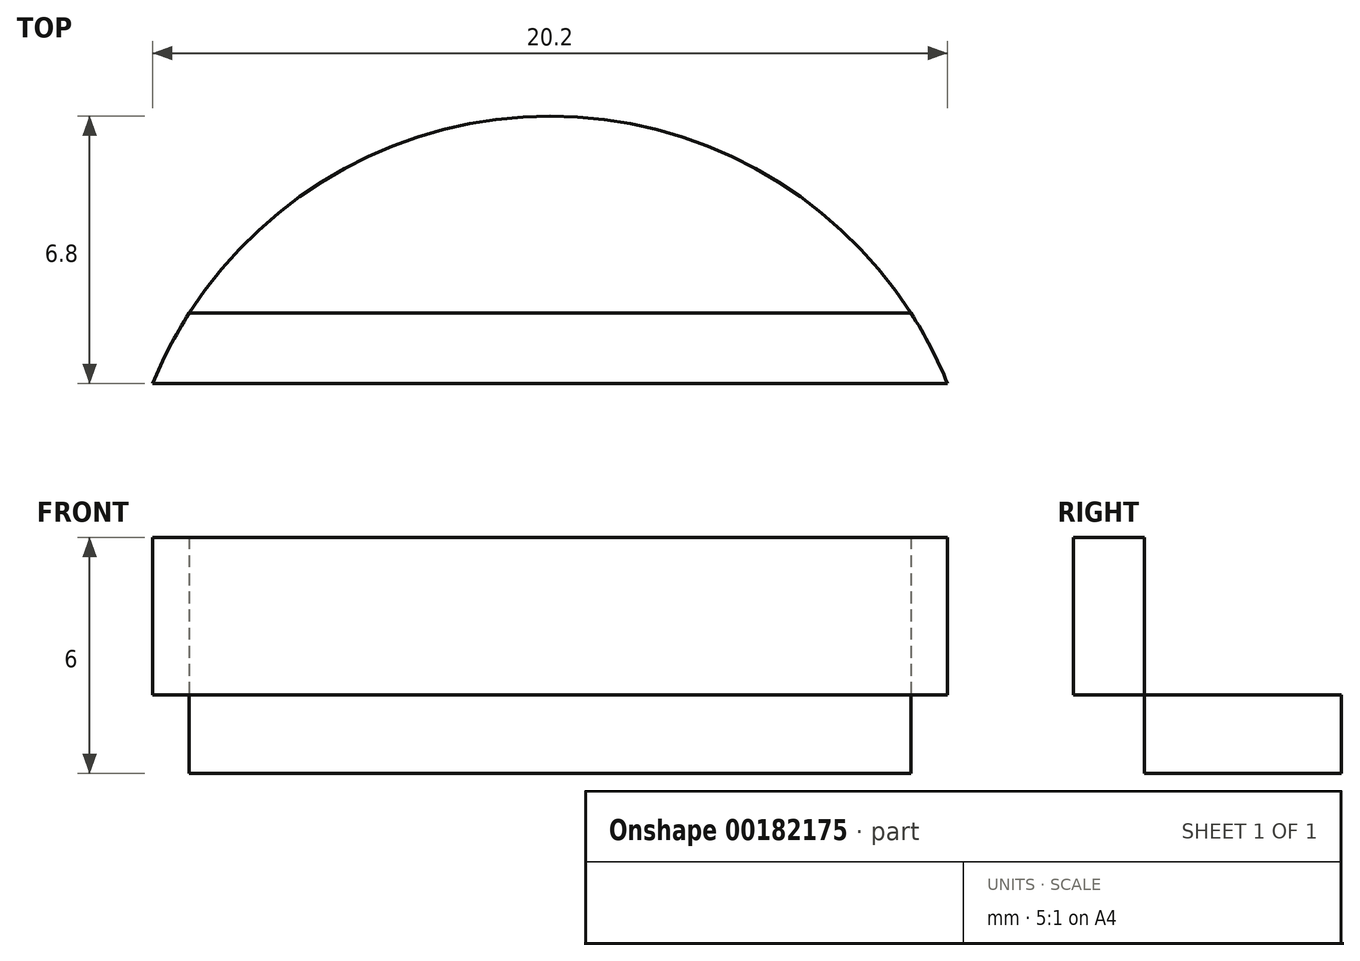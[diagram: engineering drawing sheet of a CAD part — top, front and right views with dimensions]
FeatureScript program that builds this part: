
annotation { "Feature Type Name" : "Feature", "Feature Type Description" : "" }
export const myFeature = defineFeature(function(context is Context, id is Id, definition is map)
    precondition{}
    {
        {
            var Q0;
            Q0=qCreatedBy(makeId("Top.planeOp"),FACE);
            var sketch = newSketch(context, id + "F0", { "sketchPlane" : qUnion([Q0])});
            skCircle(sketch, "E0", {"center": v(0, 0) * mm, "radius": 10.9 * mm});
            skLineSegment(sketch, "E1.bottom", {"start": v(17.66, -5.9) * mm, "end": v(-17.66, -5.9) * mm});
            skLineSegment(sketch, "E1.top", {"start": v(17.66, 5.9) * mm, "end": v(-17.66, 5.9) * mm});
            skLineSegment(sketch, "E1.left", {"start": v(17.66, -5.9) * mm, "end": v(17.66, 5.9) * mm});
            skLineSegment(sketch, "E1.right", {"start": v(-17.66, -5.9) * mm, "end": v(-17.66, 5.9) * mm});
            skSolve(sketch);
        }
        {
            var Q0;
            {var subQ0=sQuery(id+"F0.wireOp",EDGE,"E1.top");var subQ1=sQuery(id+"F0.wireOp",EDGE,"E0");var subQ2=makeQuery(id+"F0.imprint","INTERSECT",VERTEX,{"disambiguationData":[OD(0.0)],"derivedFrom":[subQ1,subQ0]});Q0=makeQuery(id+"F0.imprint","IMPRINT",FACE,{"disambiguationData":[TD([[makeQuery(id+"F0.imprint","IMPRINT",EDGE,{"disambiguationData":[TD([[subQ2,-1.0]])],"derivedFrom":subQ1}),1.0]])]});}
            extrude(context, id + "F1", {"entities" : qUnion([Q0]), "depth" : 2 * mm});
        }
        {
            var Q0;
            Q0=makeQuery(id+"F1.opExtrude","CAP_FACE",FACE,{"disambiguationData":[OSD([sQuery(id+"F0.wireOp",EDGE,"E0"),sQuery(id+"F0.wireOp",EDGE,"E1.bottom"),sQuery(id+"F0.wireOp",EDGE,"E1.top")])],"isStart":false});
            var sketch = newSketch(context, id + "F2", { "sketchPlane" : qUnion([Q0])});
            skCircle(sketch, "E2", {"center": v(0, 0) * mm, "radius": 3.55 * mm});
            skSolve(sketch);
        }
        {
            var Q0;
            Q0 = qSketchRegion(id + "F2", true);
            extrude(context, id + "F3", {"entities" : qUnion([Q0]), "operationType" : NewBodyOperationType.REMOVE, "oppositeDirection" : true, "depth" : 25 * mm});
        }
        {
            var Q0;
            Q0=makeQuery(id+"F1.opExtrude","CAP_FACE",FACE,{"disambiguationData":[OSD([sQuery(id+"F0.wireOp",EDGE,"E0"),sQuery(id+"F0.wireOp",EDGE,"E1.bottom"),sQuery(id+"F0.wireOp",EDGE,"E1.top")])],"isStart":false});
            var sketch = newSketch(context, id + "F4", { "sketchPlane" : qUnion([Q0])});
            skLineSegment(sketch, "E3.bottom", {"start": v(11.16, -4.1) * mm, "end": v(-11.16, -4.1) * mm});
            skLineSegment(sketch, "E3.top", {"start": v(11.16, 4.1) * mm, "end": v(-11.16, 4.1) * mm});
            skLineSegment(sketch, "E3.left", {"start": v(11.16, -4.1) * mm, "end": v(11.16, 4.1) * mm});
            skLineSegment(sketch, "E3.right", {"start": v(-11.16, -4.1) * mm, "end": v(-11.16, 4.1) * mm});
            skPoint(sketch, "E3.middle", {"position": v(0, 0) * mm});
            skLineSegment(sketch, "E4.0.0", {"start": v(-9.17, -5.9) * mm, "end": v(9.17, -5.9) * mm});
            skArc(sketch, "E4.0.1", {"start": v(9.17, -5.9) * mm, "mid": v(10.9, 0) * mm, "end": v(9.17, 5.9) * mm});
            skLineSegment(sketch, "E4.0.2", {"start": v(9.17, 5.9) * mm, "end": v(-9.17, 5.9) * mm});
            skArc(sketch, "E4.0.3", {"start": v(-9.17, 5.9) * mm, "mid": v(-10.9, 0) * mm, "end": v(-9.17, -5.9) * mm});
            skSolve(sketch);
        }
        {
            var Q0;
            {var subQ5=sQuery(id+"F4.wireOp",EDGE,"E4.0.2");Q0=makeQuery(id+"F4.imprint","IMPRINT",FACE,{"disambiguationData":[TD([[makeQuery(id+"F4.imprint","IMPRINT",EDGE,{"derivedFrom":subQ5}),1.0]])]});}
            var Q1;
            {var subQ5=sQuery(id+"F4.wireOp",EDGE,"E4.0.0");Q1=makeQuery(id+"F4.imprint","IMPRINT",FACE,{"disambiguationData":[TD([[makeQuery(id+"F4.imprint","IMPRINT",EDGE,{"derivedFrom":subQ5}),-1.0]])]});}
            extrude(context, id + "F5", {"entities" : qUnion([Q0, Q1]), "operationType" : NewBodyOperationType.ADD, "depth" : 4 * mm});
        }
    });
